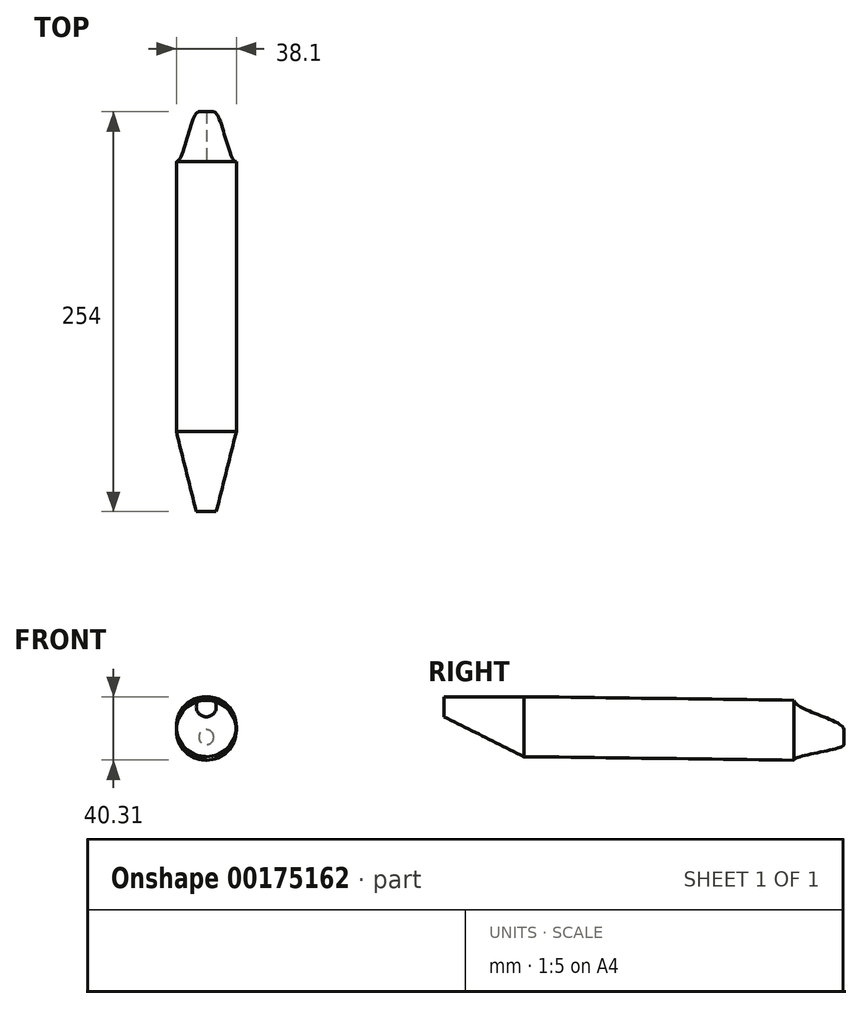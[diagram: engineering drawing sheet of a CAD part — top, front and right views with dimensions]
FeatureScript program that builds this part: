
annotation { "Feature Type Name" : "Feature", "Feature Type Description" : "" }
export const myFeature = defineFeature(function(context is Context, id is Id, definition is map)
    precondition{}
    {
        {
            var Q0;
            Q0=qCreatedBy(makeId("Front.planeOp"),FACE);
            var sketch = newSketch(context, id + "F0", { "sketchPlane" : qUnion([Q0])});
            skCircle(sketch, "E0", {"center": v(0, -6.65) * mm, "radius": 4.76 * mm});
            skSolve(sketch);
        }
        {
            var Q0;
            Q0=qCreatedBy(makeId("Front.planeOp"),FACE);
            cPlane(context, id + "F1", {"entities" : qUnion([Q0]), "cplaneType" : CPlaneType.OFFSET, "offset" : 31.75 * mm, "width" : 152.4 * mm, "height" : 152.4 * mm});
        }
        {
            var Q0;
            Q0=qCreatedBy(makeId("Front.planeOp"),FACE);
            cPlane(context, id + "F2", {"entities" : qUnion([Q0]), "cplaneType" : CPlaneType.OFFSET, "offset" : 254 * mm, "width" : 152.4 * mm, "height" : 152.4 * mm});
        }
        {
            var Q0;
            Q0=qCreatedBy(id+"F1.planeOp",FACE);
            var sketch = newSketch(context, id + "F3", { "sketchPlane" : qUnion([Q0])});
            skCircle(sketch, "E1", {"center": v(0, -2.21) * mm, "radius": 19.05 * mm});
            skSolve(sketch);
        }
        {
            var Q0;
            Q0=qCreatedBy(id+"F2.planeOp",FACE);
            var sketch = newSketch(context, id + "F4", { "sketchPlane" : qUnion([Q0])});
            skCircle(sketch, "E2", {"center": v(0, 12.6) * mm, "radius": 6.35 * mm});
            skSolve(sketch);
        }
        {
            var Q0;
            Q0=qCreatedBy(makeId("Front.planeOp"),FACE);
            cPlane(context, id + "F5", {"entities" : qUnion([Q0]), "cplaneType" : CPlaneType.OFFSET, "offset" : 203.2 * mm, "width" : 152.4 * mm, "height" : 152.4 * mm});
        }
        {
            var Q0;
            Q0=qCreatedBy(id+"F5.planeOp",FACE);
            var sketch = newSketch(context, id + "F6", { "sketchPlane" : qUnion([Q0])});
            skCircle(sketch, "E3", {"center": v(0, 0) * mm, "radius": 19.05 * mm});
            skSolve(sketch);
        }
        {
            var Q0;
            Q0=makeQuery(id+"F0.imprint","IMPRINT",FACE,{"disambiguationData":[TD([[makeQuery(id+"F0.imprint","IMPRINT",EDGE,{"derivedFrom":sQuery(id+"F0.wireOp",EDGE,"E0")}),1.0]])]});
            var Q1;
            Q1=makeQuery(id+"F3.imprint","IMPRINT",FACE,{"disambiguationData":[TD([[makeQuery(id+"F3.imprint","IMPRINT",EDGE,{"derivedFrom":sQuery(id+"F3.wireOp",EDGE,"E1")}),1.0]])]});
            loft(context, id + "F7", {"startCondition" : LoftEndDerivativeType.TANGENT_TO_PROFILE, "startMagnitude" : 1, "endCondition" : LoftEndDerivativeType.TANGENT_TO_PROFILE, "endMagnitude" : 1, "sheetProfilesArray" : [{ "sheetProfileEntities" : qUnion([Q0]) }, { "sheetProfileEntities" : qUnion([Q1]) }]});
        }
        {
            var Q0;
            Q0=makeQuery(id+"F6.imprint","IMPRINT",FACE,{"disambiguationData":[TD([[makeQuery(id+"F6.imprint","IMPRINT",EDGE,{"derivedFrom":sQuery(id+"F6.wireOp",EDGE,"E3")}),1.0]])]});
            var Q1;
            Q1=makeQuery(id+"F4.imprint","IMPRINT",FACE,{"disambiguationData":[TD([[makeQuery(id+"F4.imprint","IMPRINT",EDGE,{"derivedFrom":sQuery(id+"F4.wireOp",EDGE,"E2")}),1.0]])]});
            loft(context, id + "F8", {"sheetProfilesArray" : [{ "sheetProfileEntities" : qUnion([Q0]) }, { "sheetProfileEntities" : qUnion([Q1]) }]});
        }
        {
            var Q0;
            Q0=makeQuery(id+"F7.opLoft","CAP_FACE",FACE,{"disambiguationData":[OSD([makeQuery(id+"F3.imprint","IMPRINT",FACE,{"disambiguationData":[TD([[makeQuery(id+"F3.imprint","IMPRINT",EDGE,{"derivedFrom":sQuery(id+"F3.wireOp",EDGE,"E1")}),1.0]])]})])],"isStart":true});
            var Q1;
            Q1=makeQuery(id+"F6.imprint","IMPRINT",FACE,{"disambiguationData":[TD([[makeQuery(id+"F6.imprint","IMPRINT",EDGE,{"derivedFrom":sQuery(id+"F6.wireOp",EDGE,"E3")}),1.0]])]});
            loft(context, id + "F9", {"sheetProfilesArray" : [{ "sheetProfileEntities" : qUnion([Q0]) }, { "sheetProfileEntities" : qUnion([Q1]) }]});
        }
    });
